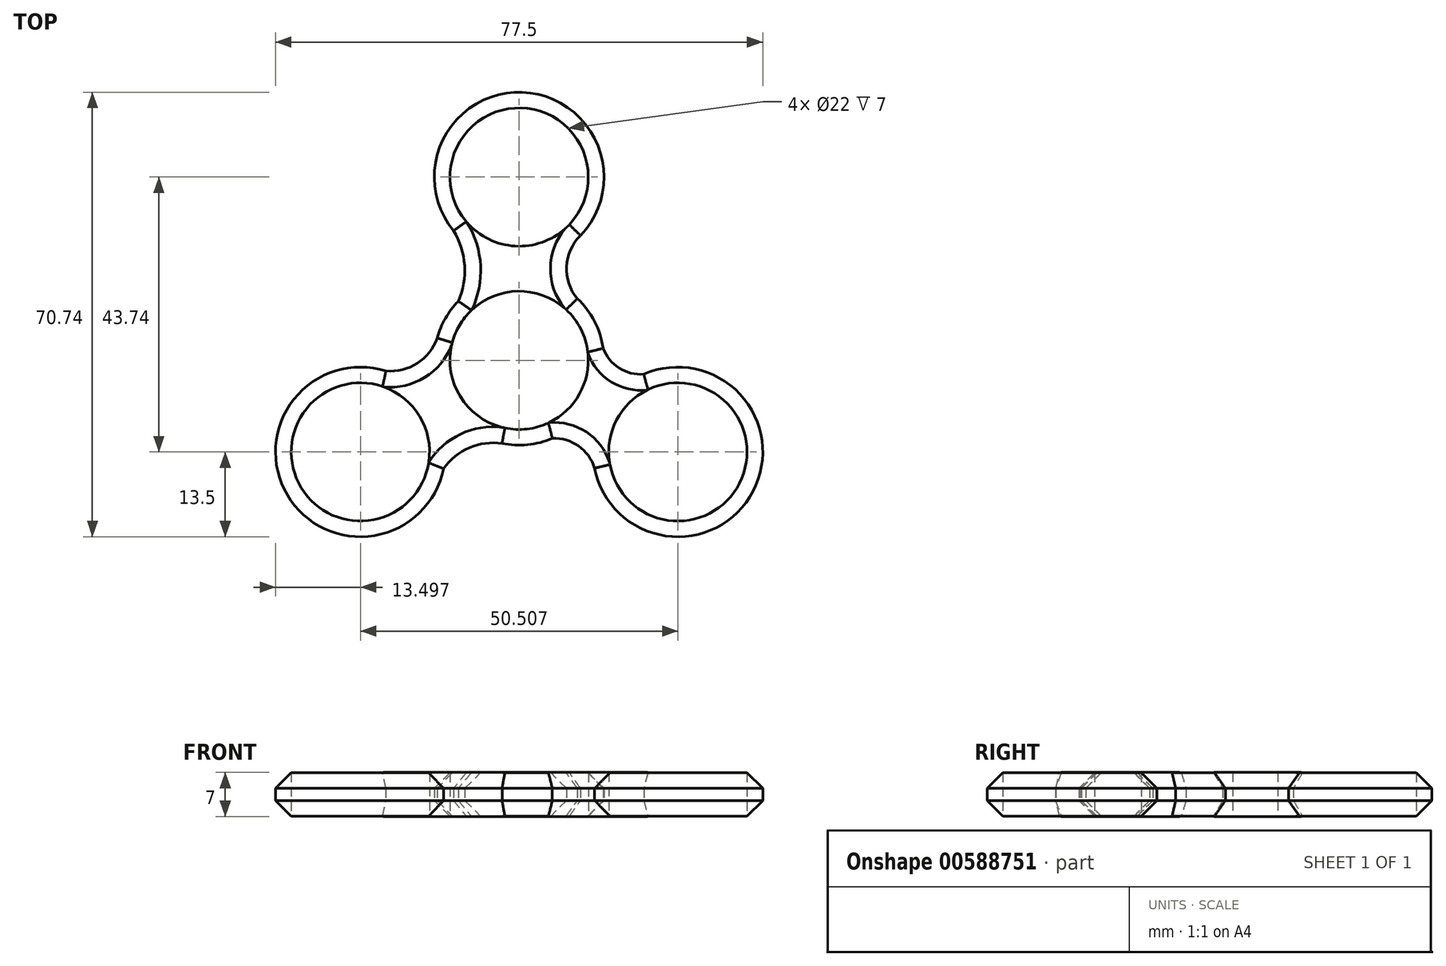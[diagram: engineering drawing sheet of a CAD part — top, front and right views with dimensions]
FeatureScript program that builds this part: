
annotation { "Feature Type Name" : "Feature", "Feature Type Description" : "" }
export const myFeature = defineFeature(function(context is Context, id is Id, definition is map)
    precondition{}
    {
        {
            var Q0;
            Q0=qCreatedBy(makeId("Top.planeOp"),FACE);
            var sketch = newSketch(context, id + "F0", { "sketchPlane" : qUnion([Q0])});
            skCircle(sketch, "E0", {"center": v(0, 0) * mm, "radius": 11 * mm});
            skCircle(sketch, "E1", {"center": v(0, 0) * mm, "radius": 13.5 * mm});
            skCircle(sketch, "E2", {"center": v(0, 29.16) * mm, "radius": 11 * mm});
            skCircle(sketch, "E3", {"center": v(0, 29.16) * mm, "radius": 13.5 * mm});
            skCircle(sketch, "E4.1.0", {"center": v(-25.25, -14.58) * mm, "radius": 11 * mm});
            skCircle(sketch, "E4.2.0", {"center": v(25.25, -14.58) * mm, "radius": 11 * mm});
            skCircle(sketch, "E5.1.0", {"center": v(-25.25, -14.58) * mm, "radius": 13.5 * mm});
            skCircle(sketch, "E5.2.0", {"center": v(25.25, -14.58) * mm, "radius": 13.5 * mm});
            skArc(sketch, "E6", {"start": v(-9.69, 9.4) * mm, "mid": v(-8.68, 15.1) * mm, "end": v(-10.44, 20.6) * mm});
            skArc(sketch, "E7", {"start": v(9.76, 19.84) * mm, "mid": v(7.53, 14.92) * mm, "end": v(9.27, 9.81) * mm});
            skArc(sketch, "E8", {"start": v(-21.2, -1.7) * mm, "mid": v(-16.22, -0.47) * mm, "end": v(-13.03, 3.55) * mm});
            skArc(sketch, "E9", {"start": v(-2.71, -13.22) * mm, "mid": v(-7.94, -13.91) * mm, "end": v(-12.02, -17.25) * mm});
            skArc(sketch, "E10", {"start": v(12, -17.17) * mm, "mid": v(9.46, -13.64) * mm, "end": v(5.28, -12.43) * mm});
            skArc(sketch, "E11", {"start": v(13.36, 1.91) * mm, "mid": v(15.92, -1.22) * mm, "end": v(19.84, -2.21) * mm});
            skSolve(sketch);
        }
        {
            var Q0;
            Q0=makeQuery(id+"F0.imprint","IMPRINT",FACE,{"disambiguationData":[TD([[makeQuery(id+"F0.imprint","IMPRINT",EDGE,{"derivedFrom":sQuery(id+"F0.wireOp",EDGE,"E2")}),-1.0]])]});
            var Q1;
            Q1=makeQuery(id+"F0.imprint","IMPRINT",FACE,{"disambiguationData":[TD([[makeQuery(id+"F0.imprint","IMPRINT",EDGE,{"derivedFrom":sQuery(id+"F0.wireOp",EDGE,"E0")}),-1.0]])]});
            var Q2;
            Q2=makeQuery(id+"F0.imprint","IMPRINT",FACE,{"disambiguationData":[TD([[makeQuery(id+"F0.imprint","IMPRINT",EDGE,{"derivedFrom":sQuery(id+"F0.wireOp",EDGE,"E4.1.0")}),-1.0]])]});
            var Q3;
            Q3=makeQuery(id+"F0.imprint","IMPRINT",FACE,{"disambiguationData":[TD([[makeQuery(id+"F0.imprint","IMPRINT",EDGE,{"derivedFrom":sQuery(id+"F0.wireOp",EDGE,"E4.2.0")}),-1.0]])]});
            var Q4;
            {var subQ0=sQuery(id+"F0.wireOp",EDGE,"E10");Q4=makeQuery(id+"F0.imprint","IMPRINT",FACE,{"disambiguationData":[TD([[makeQuery(id+"F0.imprint","IMPRINT",EDGE,{"derivedFrom":subQ0}),-1.0]])]});}
            var Q5;
            {var subQ0=sQuery(id+"F0.wireOp",EDGE,"E8");Q5=makeQuery(id+"F0.imprint","IMPRINT",FACE,{"disambiguationData":[TD([[makeQuery(id+"F0.imprint","IMPRINT",EDGE,{"derivedFrom":subQ0}),-1.0]])]});}
            var Q6;
            {var subQ0=sQuery(id+"F0.wireOp",EDGE,"E6");Q6=makeQuery(id+"F0.imprint","IMPRINT",FACE,{"disambiguationData":[TD([[makeQuery(id+"F0.imprint","IMPRINT",EDGE,{"derivedFrom":subQ0}),-1.0]])]});}
            extrude(context, id + "F1", {"entities" : qUnion([Q0, Q1, Q2, Q3, Q4, Q5, Q6]), "depth" : 7 * mm, "offsetDistance" : 25 * mm});
        }
        {
            var Q0;
            Q0=makeQuery(id+"F1.opExtrude","CAP_EDGE",EDGE,{"disambiguationData":[OSD([sQuery(id+"F0.wireOp",EDGE,"E6")])],"isStart":true});
            var Q1;
            {var subQ0=sQuery(id+"F0.wireOp",EDGE,"E1");Q1=makeQuery(id+"F1.opExtrude","CAP_EDGE",EDGE,{"disambiguationData":[OSD([subQ0]),TDD([makeQuery(id+"F0.imprint","IMPRINT",EDGE,{"disambiguationData":[TD([[makeQuery(id+"F0.imprint","INTERSECT",VERTEX,{"derivedFrom":[subQ0,sQuery(id+"F0.wireOp",EDGE,"E6")]}),-1.0]])],"derivedFrom":subQ0})])],"isStart":true});}
            var Q2;
            Q2=makeQuery(id+"F1.opExtrude","CAP_EDGE",EDGE,{"disambiguationData":[OSD([sQuery(id+"F0.wireOp",EDGE,"E8")])],"isStart":true});
            var Q3;
            Q3=makeQuery(id+"F1.opExtrude","CAP_EDGE",EDGE,{"disambiguationData":[OSD([sQuery(id+"F0.wireOp",EDGE,"E9")])],"isStart":true});
            var Q4;
            {var subQ0=sQuery(id+"F0.wireOp",EDGE,"E1");Q4=makeQuery(id+"F1.opExtrude","CAP_EDGE",EDGE,{"disambiguationData":[OSD([subQ0]),TDD([makeQuery(id+"F0.imprint","IMPRINT",EDGE,{"disambiguationData":[TD([[makeQuery(id+"F0.imprint","INTERSECT",VERTEX,{"derivedFrom":[subQ0,sQuery(id+"F0.wireOp",EDGE,"E9")]}),-1.0]])],"derivedFrom":subQ0})])],"isStart":true});}
            var Q5;
            Q5=makeQuery(id+"F1.opExtrude","CAP_EDGE",EDGE,{"disambiguationData":[OSD([sQuery(id+"F0.wireOp",EDGE,"E10")])],"isStart":true});
            var Q6;
            Q6=makeQuery(id+"F1.opExtrude","CAP_EDGE",EDGE,{"disambiguationData":[OSD([sQuery(id+"F0.wireOp",EDGE,"E11")])],"isStart":true});
            var Q7;
            {var subQ0=sQuery(id+"F0.wireOp",EDGE,"E1");Q7=makeQuery(id+"F1.opExtrude","CAP_EDGE",EDGE,{"disambiguationData":[OSD([subQ0]),TDD([makeQuery(id+"F0.imprint","IMPRINT",EDGE,{"disambiguationData":[TD([[makeQuery(id+"F0.imprint","INTERSECT",VERTEX,{"derivedFrom":[subQ0,sQuery(id+"F0.wireOp",EDGE,"E7")]}),1.0]])],"derivedFrom":subQ0})])],"isStart":true});}
            var Q8;
            Q8=makeQuery(id+"F1.opExtrude","CAP_EDGE",EDGE,{"disambiguationData":[OSD([sQuery(id+"F0.wireOp",EDGE,"E7")])],"isStart":true});
            var Q9;
            {var subQ0=sQuery(id+"F0.wireOp",EDGE,"E1");Q9=makeQuery(id+"F1.opExtrude","CAP_EDGE",EDGE,{"disambiguationData":[OSD([subQ0]),TDD([makeQuery(id+"F0.imprint","IMPRINT",EDGE,{"disambiguationData":[TD([[makeQuery(id+"F0.imprint","INTERSECT",VERTEX,{"derivedFrom":[subQ0,sQuery(id+"F0.wireOp",EDGE,"E6")]}),-1.0]])],"derivedFrom":subQ0})])],"isStart":false});}
            var Q10;
            Q10=makeQuery(id+"F1.opExtrude","CAP_EDGE",EDGE,{"disambiguationData":[OSD([sQuery(id+"F0.wireOp",EDGE,"E8")])],"isStart":false});
            var Q11;
            Q11=makeQuery(id+"F1.opExtrude","CAP_EDGE",EDGE,{"disambiguationData":[OSD([sQuery(id+"F0.wireOp",EDGE,"E6")])],"isStart":false});
            var Q12;
            Q12=makeQuery(id+"F1.opExtrude","CAP_EDGE",EDGE,{"disambiguationData":[OSD([sQuery(id+"F0.wireOp",EDGE,"E7")])],"isStart":false});
            var Q13;
            {var subQ0=sQuery(id+"F0.wireOp",EDGE,"E1");Q13=makeQuery(id+"F1.opExtrude","CAP_EDGE",EDGE,{"disambiguationData":[OSD([subQ0]),TDD([makeQuery(id+"F0.imprint","IMPRINT",EDGE,{"disambiguationData":[TD([[makeQuery(id+"F0.imprint","INTERSECT",VERTEX,{"derivedFrom":[subQ0,sQuery(id+"F0.wireOp",EDGE,"E7")]}),1.0]])],"derivedFrom":subQ0})])],"isStart":false});}
            var Q14;
            Q14=makeQuery(id+"F1.opExtrude","CAP_EDGE",EDGE,{"disambiguationData":[OSD([sQuery(id+"F0.wireOp",EDGE,"E11")])],"isStart":false});
            var Q15;
            Q15=makeQuery(id+"F1.opExtrude","CAP_EDGE",EDGE,{"disambiguationData":[OSD([sQuery(id+"F0.wireOp",EDGE,"E10")])],"isStart":false});
            var Q16;
            {var subQ0=sQuery(id+"F0.wireOp",EDGE,"E1");Q16=makeQuery(id+"F1.opExtrude","CAP_EDGE",EDGE,{"disambiguationData":[OSD([subQ0]),TDD([makeQuery(id+"F0.imprint","IMPRINT",EDGE,{"disambiguationData":[TD([[makeQuery(id+"F0.imprint","INTERSECT",VERTEX,{"derivedFrom":[subQ0,sQuery(id+"F0.wireOp",EDGE,"E9")]}),-1.0]])],"derivedFrom":subQ0})])],"isStart":false});}
            var Q17;
            Q17=makeQuery(id+"F1.opExtrude","CAP_EDGE",EDGE,{"disambiguationData":[OSD([sQuery(id+"F0.wireOp",EDGE,"E9")])],"isStart":false});
            chamfer(context, id + "F2", {"entities" : qUnion([Q0, Q1, Q2, Q3, Q4, Q5, Q6, Q7, Q8, Q9, Q10, Q11, Q12, Q13, Q14, Q15, Q16, Q17]), "width" : 2.54 * mm, "tangentPropagation" : true});
        }
        {
            var Q0;
            Q0=makeQuery(id+"F1.opExtrude","CAP_EDGE",EDGE,{"disambiguationData":[OSD([sQuery(id+"F0.wireOp",EDGE,"E5.1.0")])],"isStart":false});
            var Q1;
            Q1=makeQuery(id+"F1.opExtrude","CAP_EDGE",EDGE,{"disambiguationData":[OSD([sQuery(id+"F0.wireOp",EDGE,"E5.2.0")])],"isStart":false});
            var Q2;
            Q2=makeQuery(id+"F1.opExtrude","CAP_EDGE",EDGE,{"disambiguationData":[OSD([sQuery(id+"F0.wireOp",EDGE,"E3")])],"isStart":false});
            var Q3;
            Q3=makeQuery(id+"F1.opExtrude","CAP_EDGE",EDGE,{"disambiguationData":[OSD([sQuery(id+"F0.wireOp",EDGE,"E3")])],"isStart":true});
            var Q4;
            Q4=makeQuery(id+"F1.opExtrude","CAP_EDGE",EDGE,{"disambiguationData":[OSD([sQuery(id+"F0.wireOp",EDGE,"E5.1.0")])],"isStart":true});
            var Q5;
            Q5=makeQuery(id+"F1.opExtrude","CAP_EDGE",EDGE,{"disambiguationData":[OSD([sQuery(id+"F0.wireOp",EDGE,"E5.2.0")])],"isStart":true});
            chamfer(context, id + "F3", {"entities" : qUnion([Q0, Q1, Q2, Q3, Q4, Q5]), "width" : 2.54 * mm, "tangentPropagation" : true});
        }
    });
